# Revit family: Dropp
name_source: partatom
category: Мебель
revit_build: Autodesk Revit 2017 (Build: 20160225_1515(x64)
units: mm (PartAtom-declared; Revit-internal decimal feet)

## family parameters
Всегда вертикально = Да
Заголовок OmniClass = General Furniture and Specialties
На основе рабочей плоскости = Нет
Номер OmniClass = 23.40.20.00
Общий = Нет
При загрузке вырезать с полостями = Нет
Точка расчета площади = Нет

## types (4) — shared parameters
Ключевая пометка = XBE.1
Комментарии к типоразмеру = Created by Astacus AB
Описание = Table top inbirch, white laminate or 6 mm screened glass, chassis inchromium or silver lacquered metal.

## per-type parameters (varying)
| type | Disc | Leg | URL | Группа модели | Изготовитель |
| LB-611 - Glas | LB-611-glass | LB-611-leg | http://www.biminfo.se | LB-611 - Glas | Skandiform AB |
| LB-611 - Wood | LB-611-leg | LB-611-tree | http://www.biminfo.se | LB-611 - Trä | Skandiform AB |
| LB-610 - Wood | LB-610-tree | LB-610-leg | http://www.biminfo.se | LB-610 - Trä | Skandiform AB |
| LB-610 - Glas | LB-610-glass | LB-610-leg | http://file-system.ru | LB-610 - Glas | Skandiform |

## geometry (parser evidence)
native form markers: Blend x12, Sweep x13
no freeform markers — native parametric forms only
